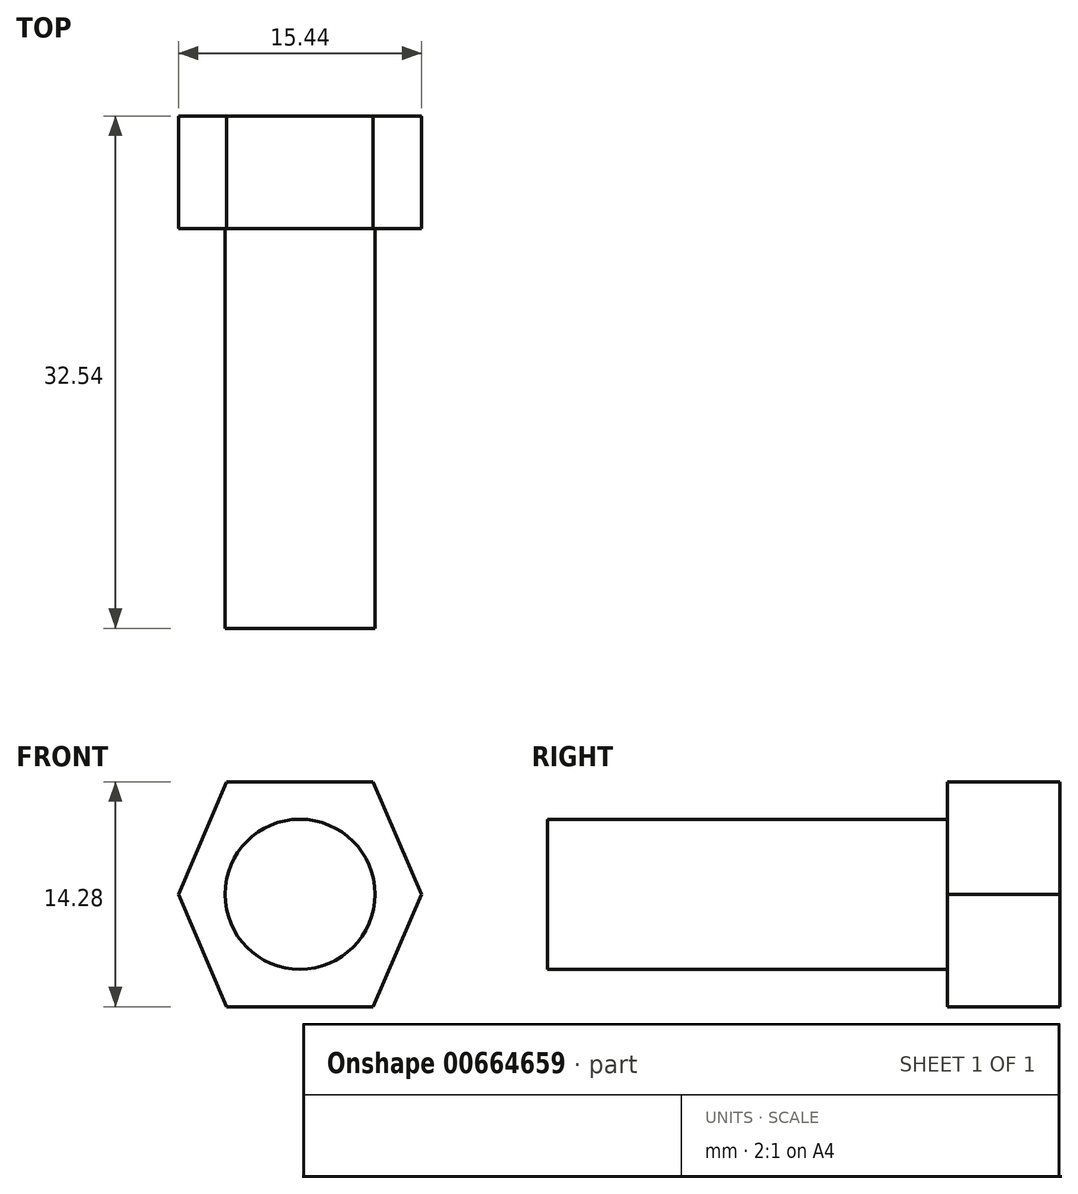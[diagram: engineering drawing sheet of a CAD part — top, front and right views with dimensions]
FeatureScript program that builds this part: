
annotation { "Feature Type Name" : "Feature", "Feature Type Description" : "" }
export const myFeature = defineFeature(function(context is Context, id is Id, definition is map)
    precondition{}
    {
        {
            var Q0;
            Q0=qCreatedBy(makeId("Front.planeOp"),FACE);
            var sketch = newSketch(context, id + "F0", { "sketchPlane" : qUnion([Q0])});
            skLineSegment(sketch, "E0", {"start": v(8.15, 7.14) * mm, "end": v(17.46, 7.14) * mm});
            skLineSegment(sketch, "E1", {"start": v(17.46, 7.14) * mm, "end": v(20.53, 0) * mm});
            skLineSegment(sketch, "E2", {"start": v(20.53, 0) * mm, "end": v(17.46, -7.14) * mm});
            skLineSegment(sketch, "E3", {"start": v(17.46, -7.14) * mm, "end": v(8.15, -7.14) * mm});
            skLineSegment(sketch, "E4", {"start": v(8.15, -7.14) * mm, "end": v(5.1, 0) * mm});
            skLineSegment(sketch, "E5", {"start": v(5.1, 0) * mm, "end": v(8.15, 7.14) * mm});
            skSolve(sketch);
        }
        {
            var Q0;
            Q0 = qSketchRegion(id + "F0", true);
            extrude(context, id + "F1", {"entities" : qUnion([Q0]), "depth" : 7.14 * mm, "offsetDistance" : 25.4 * mm});
        }
        {
            var Q0;
            Q0=makeQuery(id+"F1.opExtrude","CAP_FACE",FACE,{"disambiguationData":[OSD([sQuery(id+"F0.wireOp",EDGE,"E0"),sQuery(id+"F0.wireOp",EDGE,"E1"),sQuery(id+"F0.wireOp",EDGE,"E2"),sQuery(id+"F0.wireOp",EDGE,"E3"),sQuery(id+"F0.wireOp",EDGE,"E4"),sQuery(id+"F0.wireOp",EDGE,"E5")])],"isStart":false});
            var sketch = newSketch(context, id + "F2", { "sketchPlane" : qUnion([Q0])});
            skCircle(sketch, "E6", {"center": v(12.8, 0) * mm, "radius": 4.76 * mm});
            skPoint(sketch, "E6.centerSnap0", {"position": v(12.8, 7.14) * mm});
            skSolve(sketch);
        }
        {
            var Q0;
            Q0 = qSketchRegion(id + "F2", true);
            extrude(context, id + "F3", {"entities" : qUnion([Q0]), "operationType" : NewBodyOperationType.ADD, "depth" : 25.4 * mm, "offsetDistance" : 25.4 * mm});
        }
    });
